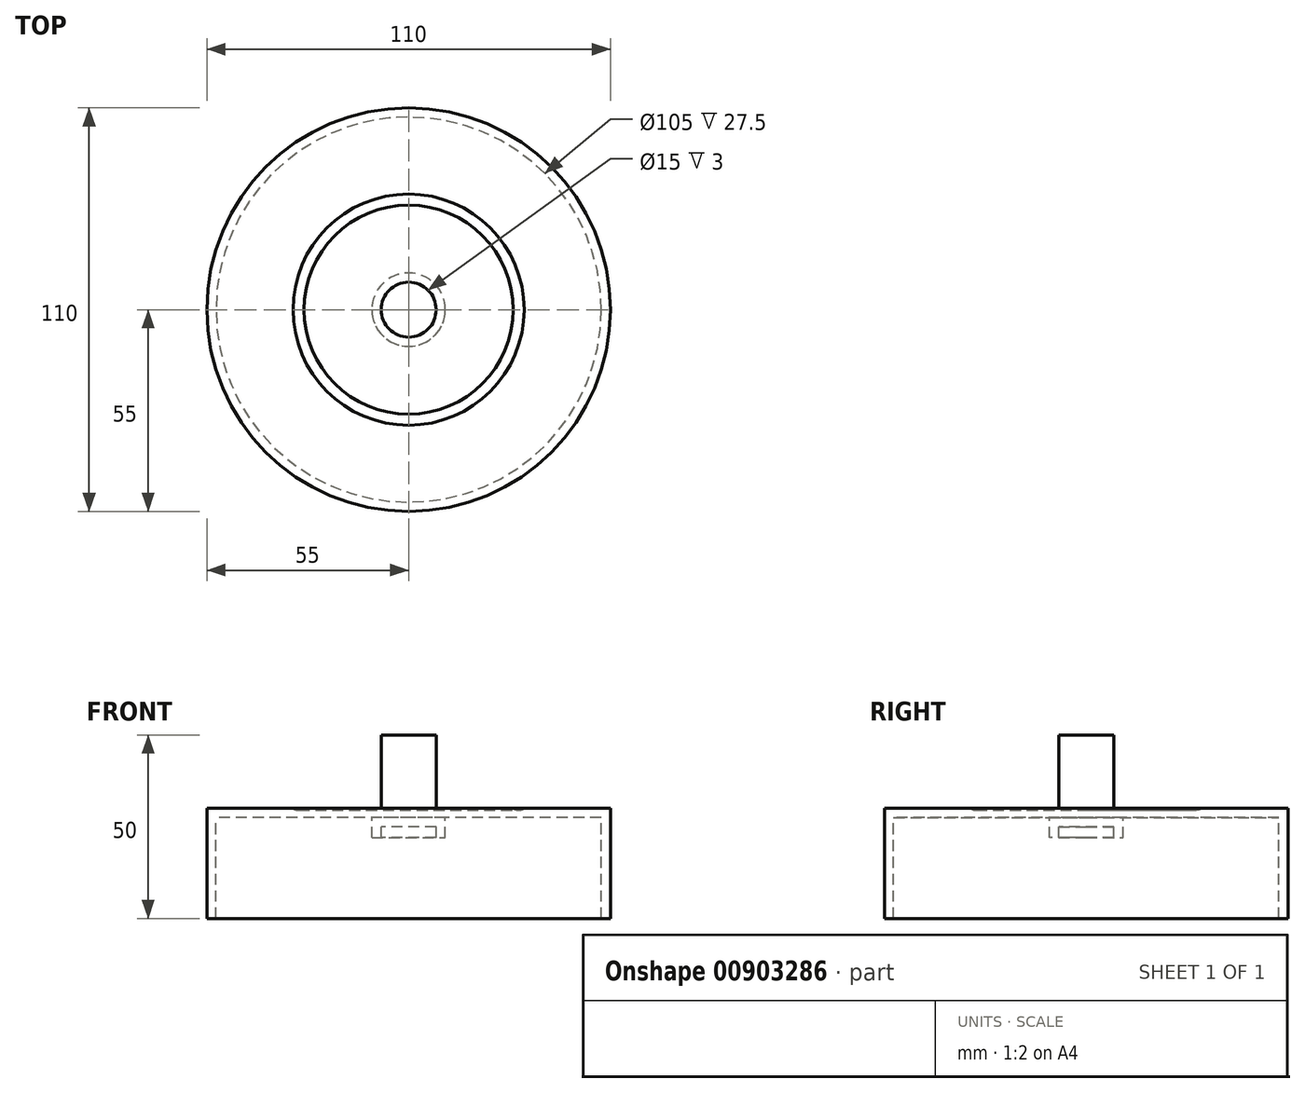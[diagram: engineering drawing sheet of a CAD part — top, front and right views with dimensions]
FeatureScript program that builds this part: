
annotation { "Feature Type Name" : "Feature", "Feature Type Description" : "" }
export const myFeature = defineFeature(function(context is Context, id is Id, definition is map)
    precondition{}
    {
        {
            var Q0;
            Q0=qCreatedBy(makeId("Top.planeOp"),FACE);
            var sketch = newSketch(context, id + "F0", { "sketchPlane" : qUnion([Q0])});
            skCircle(sketch, "E0", {"center": v(0, 0) * mm, "radius": 55 * mm});
            skCircle(sketch, "E1", {"center": v(0, 0) * mm, "radius": 7.5 * mm});
            skSolve(sketch);
        }
        {
            var Q0;
            Q0=makeQuery(id+"F0.imprint","IMPRINT",FACE,{"disambiguationData":[TD([[makeQuery(id+"F0.imprint","IMPRINT",EDGE,{"derivedFrom":sQuery(id+"F0.wireOp",EDGE,"E0")}),1.0]])]});
            extrude(context, id + "F1", {"entities" : qUnion([Q0]), "oppositeDirection" : true, "depth" : 30 * mm, "offsetDistance" : 25 * mm});
        }
        {
            var Q0;
            Q0=makeQuery(id+"F1.opExtrude","CAP_FACE",FACE,{"disambiguationData":[OSD([sQuery(id+"F0.wireOp",EDGE,"E0"),sQuery(id+"F0.wireOp",EDGE,"E1")])],"isStart":false});
            var Q1;
            Q1=makeQuery(id+"F1.opExtrude","SWEPT_FACE",FACE,{"disambiguationData":[OSD([sQuery(id+"F0.wireOp",EDGE,"E1")])]});
            shell(context, id + "F2", {"entities" : qUnion([Q0, Q1]), "thickness" : 2.5 * mm});
        }
        {
            var Q0;
            Q0=makeQuery(id+"F1.opExtrude","CAP_FACE",FACE,{"disambiguationData":[OSD([sQuery(id+"F0.wireOp",EDGE,"E0"),sQuery(id+"F0.wireOp",EDGE,"E1")])],"isStart":true});
            var sketch = newSketch(context, id + "F3", { "sketchPlane" : qUnion([Q0])});
            skCircle(sketch, "E2", {"center": v(0, 0) * mm, "radius": 30 * mm});
            skSolve(sketch);
        }
        {
            var Q0;
            Q0=qCreatedBy(makeId("Front.planeOp"),FACE);
            var sketch = newSketch(context, id + "F4", { "sketchPlane" : qUnion([Q0])});
            skLineSegment(sketch, "E3", {"start": v(0, 0) * mm, "end": v(30, 0) * mm, "construction": true});
            skLineSegment(sketch, "E4", {"start": v(30, 0) * mm, "end": v(30, 2) * mm, "construction": true});
            skCircle(sketch, "E5", {"center": v(30, 2) * mm, "radius": 2.5 * mm});
            skSolve(sketch);
        }
        {
            var Q0;
            Q0=makeQuery(id+"F4.imprint","IMPRINT",FACE,{"disambiguationData":[TD([[makeQuery(id+"F4.imprint","IMPRINT",EDGE,{"derivedFrom":sQuery(id+"F4.wireOp",EDGE,"E5")}),1.0]])]});
            var Q1;
            Q1=sQuery(id+"F3.wireOp",EDGE,"E2");
            sweep(context, id + "F5", {"operationType" : NewBodyOperationType.REMOVE, "profiles" : qUnion([Q0]), "path" : qUnion([Q1])});
        }
        {
            var Q0;
            Q0=makeQuery(id+"F3.imprint","IMPRINT",FACE,{"disambiguationData":[TD([[makeQuery(id+"F3.imprint","IMPRINT",EDGE,{"derivedFrom":makeQuery(id+"F1.opExtrude","CAP_EDGE",EDGE,{"disambiguationData":[OSD([sQuery(id+"F0.wireOp",EDGE,"E1")])],"isStart":true})}),1.0]])]});
            extrude(context, id + "F6", {"entities" : qUnion([Q0]), "depth" : 20 * mm, "offsetDistance" : 25 * mm, "hasSecondDirection" : true, "secondDirectionOppositeDirection" : true, "secondDirectionDepth" : 5 * mm});
        }
        {
            var Q0;
            Q0=makeQuery(id+"F2.opShell","OFFSET_FACE",FACE,{"disambiguationData":[OSD([sQuery(id+"F0.wireOp",EDGE,"E0"),sQuery(id+"F0.wireOp",EDGE,"E1")])]});
            var sketch = newSketch(context, id + "F7", { "sketchPlane" : qUnion([Q0])});
            skCircle(sketch, "E6", {"center": v(0, 0) * mm, "radius": 10 * mm});
            skSolve(sketch);
        }
        {
            var Q0;
            Q0=makeQuery(id+"F7.imprint","IMPRINT",FACE,{"disambiguationData":[TD([[makeQuery(id+"F7.imprint","IMPRINT",EDGE,{"derivedFrom":sQuery(id+"F7.wireOp",EDGE,"E6")}),1.0]])]});
            var Q1;
            Q1=sQuery(id+"F7.wireOp",EDGE,"E6");
            extrude(context, id + "F8", {"entities" : qUnion([Q0]), "operationType" : NewBodyOperationType.ADD, "surfaceEntities" : qUnion([Q1]), "depth" : 5.5 * mm, "offsetDistance" : 25 * mm});
        }
    });
